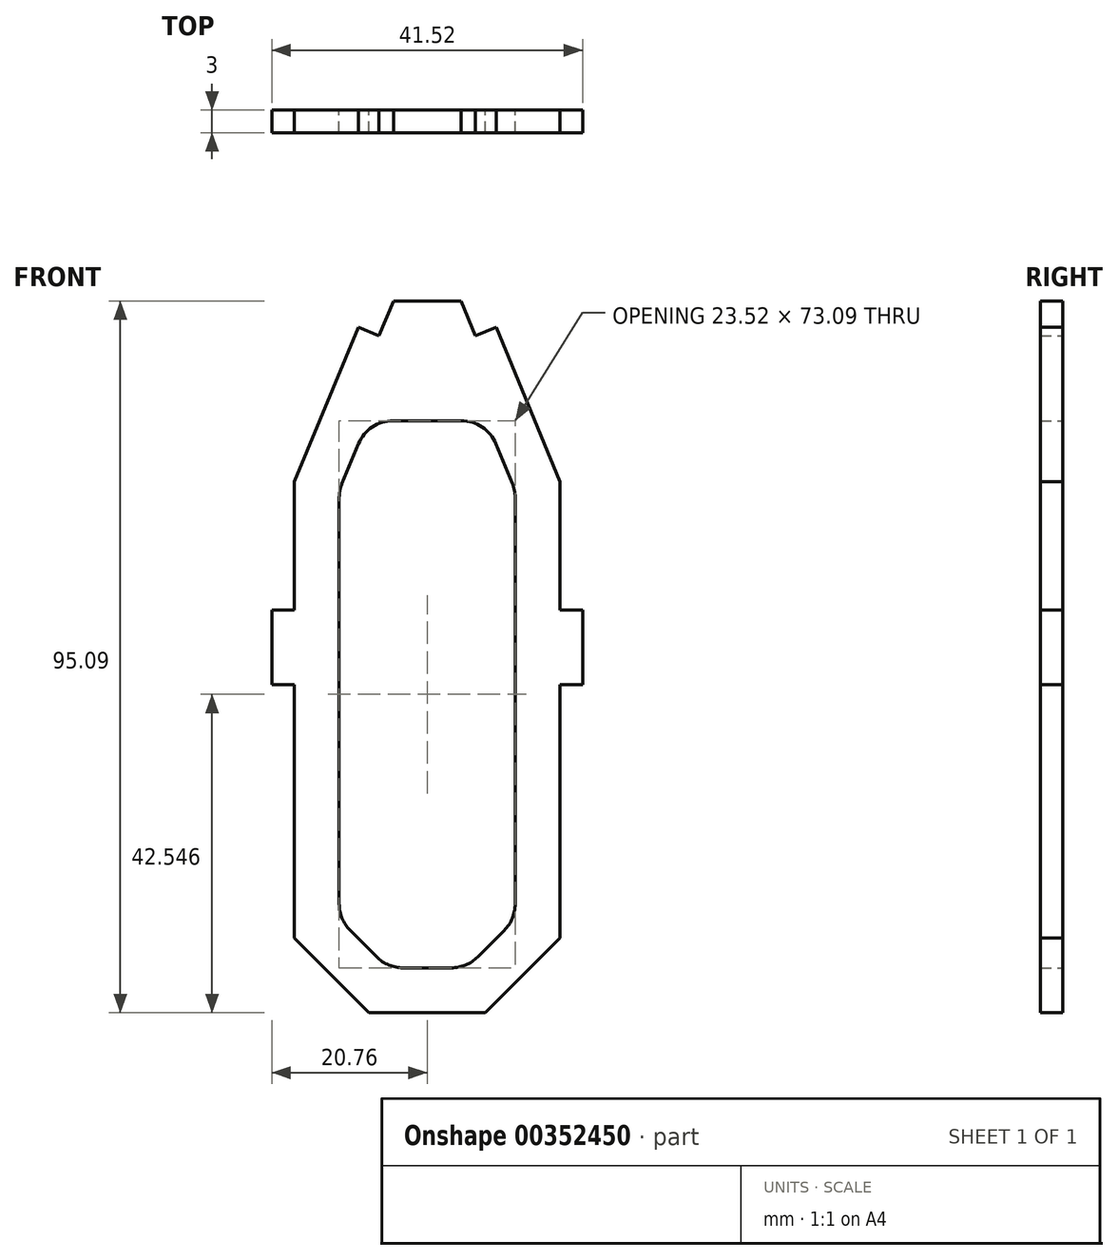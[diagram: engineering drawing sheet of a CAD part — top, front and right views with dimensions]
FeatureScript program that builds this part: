
annotation { "Feature Type Name" : "Feature", "Feature Type Description" : "" }
export const myFeature = defineFeature(function(context is Context, id is Id, definition is map)
    precondition{}
    {
        {
            var Q0;
            Q0=qCreatedBy(makeId("Front.planeOp"),FACE);
            var sketch = newSketch(context, id + "F0", { "sketchPlane" : qUnion([Q0])});
            skLineSegment(sketch, "E0", {"start": v(-17.76, 22.17) * mm, "end": v(-17.76, 5) * mm});
            skLineSegment(sketch, "E1", {"start": v(-17.76, -38.8) * mm, "end": v(-7.76, -48.8) * mm});
            skLineSegment(sketch, "E2", {"start": v(-17.76, 22.17) * mm, "end": v(-9.2, 42.81) * mm});
            skLineSegment(sketch, "E3", {"start": v(-9.2, 42.81) * mm, "end": v(-6.43, 41.66) * mm});
            skLineSegment(sketch, "E4", {"start": v(-6.43, 41.66) * mm, "end": v(-4.51, 46.28) * mm});
            skLineSegment(sketch, "E5.MirrorCS", {"start": v(6.43, 41.66) * mm, "end": v(4.51, 46.28) * mm});
            skLineSegment(sketch, "E6.MirrorCS", {"start": v(9.2, 42.81) * mm, "end": v(6.43, 41.66) * mm});
            skLineSegment(sketch, "E7.MirrorCS", {"start": v(17.76, 22.17) * mm, "end": v(17.76, 5) * mm});
            skLineSegment(sketch, "E8.MirrorCS", {"start": v(17.76, 22.17) * mm, "end": v(9.2, 42.81) * mm});
            skLineSegment(sketch, "E9.MirrorCS", {"start": v(17.76, -38.8) * mm, "end": v(7.76, -48.8) * mm});
            skLineSegment(sketch, "E10.0", {"start": v(11.38, 21.9) * mm, "end": v(9.18, 27.2) * mm});
            skLineSegment(sketch, "E10.3", {"start": v(-10.3, -37.79) * mm, "end": v(-6.74, -41.34) * mm});
            skLineSegment(sketch, "E10.4", {"start": v(-3.2, -42.8) * mm, "end": v(0, -42.8) * mm});
            skLineSegment(sketch, "E10.5", {"start": v(0, -42.8) * mm, "end": v(3.2, -42.8) * mm});
            skLineSegment(sketch, "E10.6", {"start": v(10.3, -37.79) * mm, "end": v(6.74, -41.34) * mm});
            skLineSegment(sketch, "E10.7", {"start": v(-11.76, 19.98) * mm, "end": v(-11.76, -34.25) * mm});
            skLineSegment(sketch, "E10.8", {"start": v(-11.38, 21.9) * mm, "end": v(-9.18, 27.2) * mm});
            skLineSegment(sketch, "E10.10", {"start": v(11.76, 19.98) * mm, "end": v(11.76, -34.25) * mm});
            skLineSegment(sketch, "E11", {"start": v(-4.56, 30.28) * mm, "end": v(4.56, 30.28) * mm});
            skArc(sketch, "E12.filletArc", {"start": v(-4.56, 30.28) * mm, "mid": v(-7.34, 29.44) * mm, "end": v(-9.18, 27.2) * mm});
            skArc(sketch, "E13.filletArc", {"start": v(9.18, 27.2) * mm, "mid": v(7.34, 29.44) * mm, "end": v(4.56, 30.28) * mm});
            skArc(sketch, "E14.filletArc", {"start": v(-11.76, -34.25) * mm, "mid": v(-11.38, -36.17) * mm, "end": v(-10.3, -37.79) * mm});
            skArc(sketch, "E15.filletArc", {"start": v(-6.74, -41.34) * mm, "mid": v(-5.12, -42.43) * mm, "end": v(-3.2, -42.8) * mm});
            skArc(sketch, "E16.filletArc", {"start": v(3.2, -42.8) * mm, "mid": v(5.12, -42.43) * mm, "end": v(6.74, -41.34) * mm});
            skArc(sketch, "E17.filletArc", {"start": v(10.3, -37.79) * mm, "mid": v(11.38, -36.17) * mm, "end": v(11.76, -34.25) * mm});
            skArc(sketch, "E18.filletArc", {"start": v(11.76, 19.98) * mm, "mid": v(11.66, 20.96) * mm, "end": v(11.38, 21.9) * mm});
            skArc(sketch, "E19.filletArc", {"start": v(-11.38, 21.9) * mm, "mid": v(-11.66, 20.96) * mm, "end": v(-11.76, 19.98) * mm});
            skLineSegment(sketch, "E20", {"start": v(-4.51, 46.28) * mm, "end": v(4.51, 46.28) * mm});
            skLineSegment(sketch, "E21", {"start": v(-7.76, -48.8) * mm, "end": v(7.76, -48.8) * mm});
            skLineSegment(sketch, "E22", {"start": v(0, 30.28) * mm, "end": v(0, -42.8) * mm, "construction": true});
            skLineSegment(sketch, "E23", {"start": v(-17.76, 5) * mm, "end": v(-20.76, 5) * mm});
            skLineSegment(sketch, "E24", {"start": v(-20.76, 5) * mm, "end": v(-20.76, -5) * mm});
            skLineSegment(sketch, "E25", {"start": v(-20.76, -5) * mm, "end": v(-17.76, -5) * mm});
            skLineSegment(sketch, "E26.trimOffspring", {"start": v(-17.76, -5) * mm, "end": v(-17.76, -38.8) * mm});
            skLineSegment(sketch, "E27.MirrorCS", {"start": v(17.76, 5) * mm, "end": v(20.76, 5) * mm});
            skLineSegment(sketch, "E28.MirrorCS", {"start": v(20.76, 5) * mm, "end": v(20.76, -5) * mm});
            skLineSegment(sketch, "E29.MirrorCS", {"start": v(20.76, -5) * mm, "end": v(17.76, -5) * mm});
            skLineSegment(sketch, "E30.trimOffspring", {"start": v(17.76, -5) * mm, "end": v(17.76, -38.8) * mm});
            skSolve(sketch);
        }
        {
            var Q0;
            Q0=makeQuery(id+"F0.imprint","IMPRINT",FACE,{"disambiguationData":[TD([[makeQuery(id+"F0.imprint","IMPRINT",EDGE,{"derivedFrom":sQuery(id+"F0.wireOp",EDGE,"E0")}),1.0]])]});
            extrude(context, id + "F1", {"entities" : qUnion([Q0]), "depth" : 3 * mm, "symmetric" : true});
        }
    });
